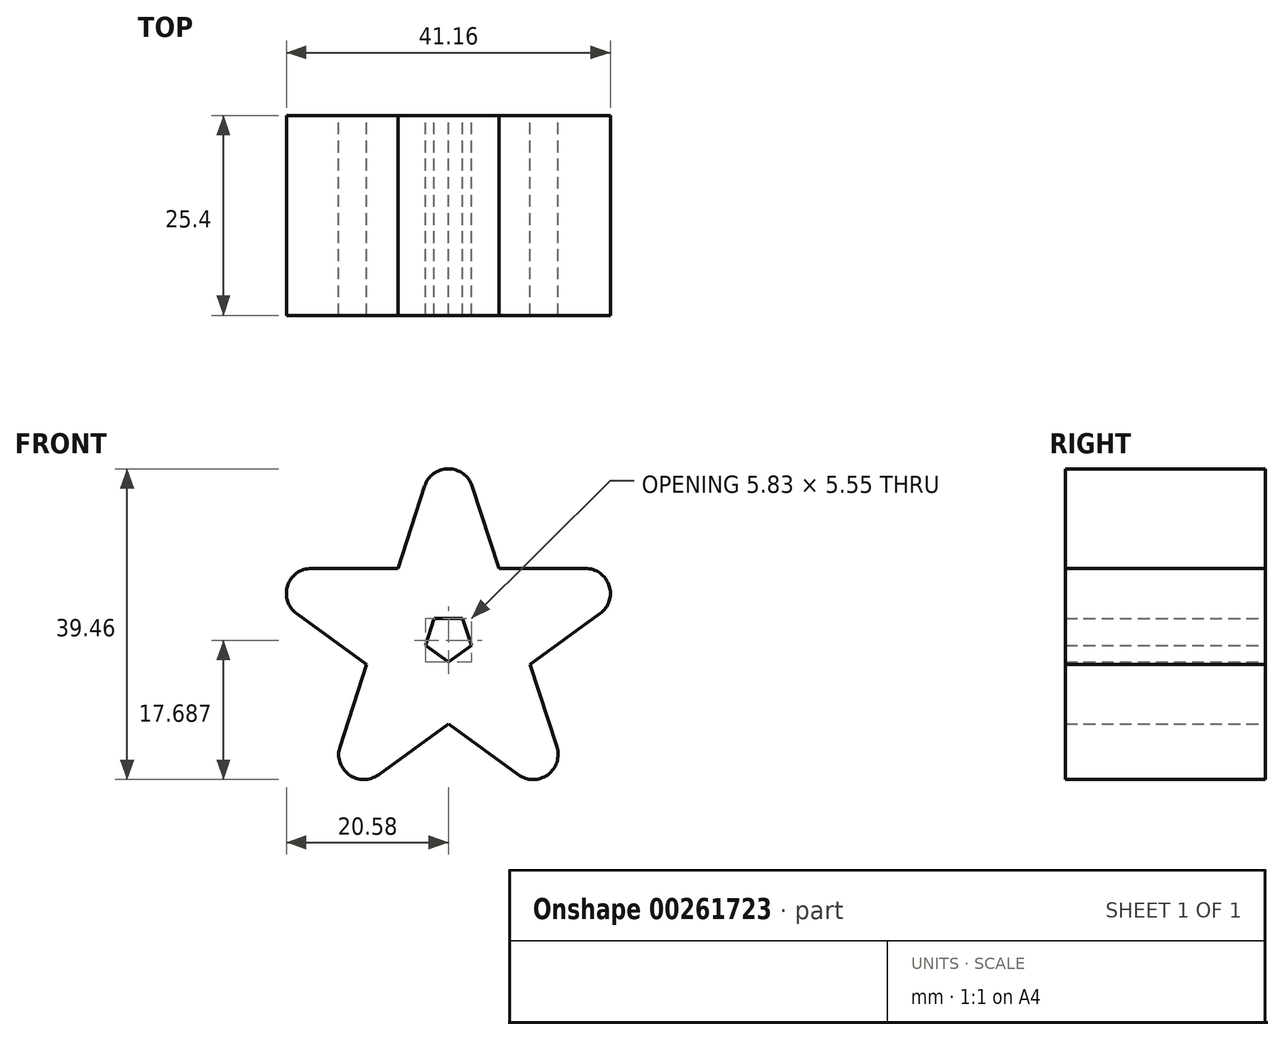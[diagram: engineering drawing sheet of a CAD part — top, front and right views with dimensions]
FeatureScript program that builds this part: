
annotation { "Feature Type Name" : "Feature", "Feature Type Description" : "" }
export const myFeature = defineFeature(function(context is Context, id is Id, definition is map)
    precondition{}
    {
        {
            var Q0;
            Q0=qCreatedBy(makeId("Front.planeOp"),FACE);
            var sketch = newSketch(context, id + "F0", { "sketchPlane" : qUnion([Q0])});
            skCircle(sketch, "E0", {"center": v(0, 18.3) * mm, "radius": 3.18 * mm});
            skCircle(sketch, "E1", {"center": v(-10.76, -14.8) * mm, "radius": 3.18 * mm});
            skCircle(sketch, "E2", {"center": v(10.76, -14.8) * mm, "radius": 3.18 * mm});
            skCircle(sketch, "E3", {"center": v(-17.4, 5.66) * mm, "radius": 3.18 * mm});
            skCircle(sketch, "E4", {"center": v(17.4, 5.66) * mm, "radius": 3.18 * mm});
            skLineSegment(sketch, "E5", {"start": v(-3.02, 19.28) * mm, "end": v(-13.78, -13.82) * mm});
            skLineSegment(sketch, "E6", {"start": v(-7.74, -15.79) * mm, "end": v(3.02, 17.32) * mm});
            skLineSegment(sketch, "E7", {"start": v(7.74, -15.79) * mm, "end": v(-3.02, 17.32) * mm});
            skLineSegment(sketch, "E8", {"start": v(3.02, 19.28) * mm, "end": v(13.78, -13.82) * mm});
            skLineSegment(sketch, "E9", {"start": v(8.9, -17.37) * mm, "end": v(-19.27, 3.09) * mm});
            skLineSegment(sketch, "E10", {"start": v(-15.54, 8.22) * mm, "end": v(12.62, -12.24) * mm});
            skLineSegment(sketch, "E11", {"start": v(-17.4, 8.83) * mm, "end": v(17.4, 8.83) * mm});
            skLineSegment(sketch, "E12", {"start": v(-17.4, 2.48) * mm, "end": v(17.4, 2.48) * mm});
            skLineSegment(sketch, "E13", {"start": v(19.27, 3.09) * mm, "end": v(-8.9, -17.37) * mm});
            skLineSegment(sketch, "E14", {"start": v(-12.62, -12.24) * mm, "end": v(15.54, 8.22) * mm});
            skCircle(sketch, "E15", {"center": v(0, 0) * mm, "radius": 21.48 * mm});
            skCircle(sketch, "E16", {"center": v(0, 0) * mm, "radius": 28.58 * mm});
            skLineSegment(sketch, "E17", {"start": v(-3.02, 19.28) * mm, "end": v(0, 28.57) * mm});
            skLineSegment(sketch, "E18", {"start": v(3.02, 19.28) * mm, "end": v(0, 28.57) * mm});
            skSolve(sketch);
        }
        {
            var Q0;
            {var subQ0=sQuery(id+"F0.wireOp",EDGE,"E0");var subQ1=makeQuery(id+"F0.imprint","INTERSECT",VERTEX,{"derivedFrom":[subQ0,sQuery(id+"F0.wireOp",EDGE,"E6")]});Q0=makeQuery(id+"F0.imprint","IMPRINT",FACE,{"disambiguationData":[TD([[makeQuery(id+"F0.imprint","IMPRINT",EDGE,{"disambiguationData":[TD([[subQ1,1.0]])],"derivedFrom":subQ0}),1.0]])]});}
            var Q1;
            {var subQ0=sQuery(id+"F0.wireOp",EDGE,"E6");var subQ1=sQuery(id+"F0.wireOp",EDGE,"E0");var subQ2=makeQuery(id+"F0.imprint","INTERSECT",VERTEX,{"derivedFrom":[subQ1,subQ0]});Q1=makeQuery(id+"F0.imprint","IMPRINT",FACE,{"disambiguationData":[TD([[makeQuery(id+"F0.imprint","IMPRINT",EDGE,{"disambiguationData":[TD([[subQ2,1.0]])],"derivedFrom":subQ1}),-1.0]])]});}
            var Q2;
            {var subQ1=sQuery(id+"F0.wireOp",EDGE,"E0");var subQ3=sQuery(id+"F0.wireOp",EDGE,"E7");var subQ4=makeQuery(id+"F0.imprint","INTERSECT",VERTEX,{"derivedFrom":[subQ1,subQ3]});Q2=makeQuery(id+"F0.imprint","IMPRINT",FACE,{"disambiguationData":[TD([[makeQuery(id+"F0.imprint","IMPRINT",EDGE,{"disambiguationData":[TD([[subQ4,1.0]])],"derivedFrom":subQ3}),1.0]])]});}
            var Q3;
            {var subQ1=sQuery(id+"F0.wireOp",EDGE,"E5");var subQ8=sQuery(id+"F0.wireOp",EDGE,"E11");var subQ11=makeQuery(id+"F0.imprint","INTERSECT",VERTEX,{"derivedFrom":[subQ1,subQ8]});Q3=makeQuery(id+"F0.imprint","IMPRINT",FACE,{"disambiguationData":[TD([[makeQuery(id+"F0.imprint","IMPRINT",EDGE,{"disambiguationData":[TD([[subQ11,-1.0]])],"derivedFrom":subQ1}),1.0]])]});}
            var Q4;
            {var subQ0=sQuery(id+"F0.wireOp",EDGE,"E10");var subQ1=sQuery(id+"F0.wireOp",EDGE,"E6");var subQ2=makeQuery(id+"F0.imprint","INTERSECT",VERTEX,{"derivedFrom":[subQ1,subQ0]});Q4=makeQuery(id+"F0.imprint","IMPRINT",FACE,{"disambiguationData":[TD([[makeQuery(id+"F0.imprint","IMPRINT",EDGE,{"disambiguationData":[TD([[subQ2,-1.0]])],"derivedFrom":subQ1}),1.0]])]});}
            var Q5;
            {var subQ3=sQuery(id+"F0.wireOp",EDGE,"E12");var subQ5=sQuery(id+"F0.wireOp",EDGE,"E5");var subQ6=makeQuery(id+"F0.imprint","INTERSECT",VERTEX,{"derivedFrom":[subQ5,subQ3]});Q5=makeQuery(id+"F0.imprint","IMPRINT",FACE,{"disambiguationData":[TD([[makeQuery(id+"F0.imprint","IMPRINT",EDGE,{"disambiguationData":[TD([[subQ6,-1.0]])],"derivedFrom":subQ5}),1.0]])]});}
            var Q6;
            {var subQ0=sQuery(id+"F0.wireOp",EDGE,"E5");var subQ1=sQuery(id+"F0.wireOp",EDGE,"E1");var subQ2=makeQuery(id+"F0.imprint","INTERSECT",VERTEX,{"derivedFrom":[subQ1,subQ0]});Q6=makeQuery(id+"F0.imprint","IMPRINT",FACE,{"disambiguationData":[TD([[makeQuery(id+"F0.imprint","IMPRINT",EDGE,{"disambiguationData":[TD([[subQ2,1.0]])],"derivedFrom":subQ1}),-1.0]])]});}
            var Q7;
            {var subQ0=sQuery(id+"F0.wireOp",EDGE,"E6");var subQ1=sQuery(id+"F0.wireOp",EDGE,"E1");var subQ2=makeQuery(id+"F0.imprint","INTERSECT",VERTEX,{"derivedFrom":[subQ1,subQ0]});Q7=makeQuery(id+"F0.imprint","IMPRINT",FACE,{"disambiguationData":[TD([[makeQuery(id+"F0.imprint","IMPRINT",EDGE,{"disambiguationData":[TD([[subQ2,-1.0]])],"derivedFrom":subQ1}),-1.0]])]});}
            var Q8;
            {var subQ0=sQuery(id+"F0.wireOp",EDGE,"E1");var subQ4=makeQuery(id+"F0.imprint","INTERSECT",VERTEX,{"derivedFrom":[subQ0,sQuery(id+"F0.wireOp",EDGE,"E5")]});Q8=makeQuery(id+"F0.imprint","IMPRINT",FACE,{"disambiguationData":[TD([[makeQuery(id+"F0.imprint","IMPRINT",EDGE,{"disambiguationData":[TD([[subQ4,1.0]])],"derivedFrom":subQ0}),1.0]])]});}
            var Q9;
            {var subQ0=sQuery(id+"F0.wireOp",EDGE,"E7");var subQ1=sQuery(id+"F0.wireOp",EDGE,"E6");var subQ2=makeQuery(id+"F0.imprint","INTERSECT",VERTEX,{"derivedFrom":[subQ1,subQ0]});Q9=makeQuery(id+"F0.imprint","IMPRINT",FACE,{"disambiguationData":[TD([[makeQuery(id+"F0.imprint","IMPRINT",EDGE,{"disambiguationData":[TD([[subQ2,-1.0]])],"derivedFrom":subQ1}),1.0]])]});}
            var Q10;
            {var subQ0=sQuery(id+"F0.wireOp",EDGE,"E9");var subQ1=sQuery(id+"F0.wireOp",EDGE,"E6");var subQ2=makeQuery(id+"F0.imprint","INTERSECT",VERTEX,{"derivedFrom":[subQ1,subQ0]});Q10=makeQuery(id+"F0.imprint","IMPRINT",FACE,{"disambiguationData":[TD([[makeQuery(id+"F0.imprint","IMPRINT",EDGE,{"disambiguationData":[TD([[subQ2,-1.0]])],"derivedFrom":subQ1}),1.0]])]});}
            var Q11;
            {var subQ0=sQuery(id+"F0.wireOp",EDGE,"E10");var subQ1=sQuery(id+"F0.wireOp",EDGE,"E5");var subQ2=makeQuery(id+"F0.imprint","INTERSECT",VERTEX,{"derivedFrom":[subQ1,subQ0]});Q11=makeQuery(id+"F0.imprint","IMPRINT",FACE,{"disambiguationData":[TD([[makeQuery(id+"F0.imprint","IMPRINT",EDGE,{"disambiguationData":[TD([[subQ2,-1.0]])],"derivedFrom":subQ1}),1.0]])]});}
            extrude(context, id + "F1", {"entities" : qUnion([Q0, Q1, Q2, Q3, Q4, Q5, Q6, Q7, Q8, Q9, Q10, Q11]), "depth" : 25.4 * mm});
        }
        {
            var Q0;
            {var subQ0=sQuery(id+"F0.wireOp",EDGE,"E3");var subQ5=makeQuery(id+"F0.imprint","INTERSECT",VERTEX,{"derivedFrom":[subQ0,sQuery(id+"F0.wireOp",EDGE,"E10")]});Q0=makeQuery(id+"F0.imprint","IMPRINT",FACE,{"disambiguationData":[TD([[makeQuery(id+"F0.imprint","IMPRINT",EDGE,{"disambiguationData":[TD([[subQ5,-1.0]])],"derivedFrom":subQ0}),1.0]])]});}
            var Q1;
            {var subQ0=sQuery(id+"F0.wireOp",EDGE,"E10");var subQ1=sQuery(id+"F0.wireOp",EDGE,"E3");var subQ2=makeQuery(id+"F0.imprint","INTERSECT",VERTEX,{"derivedFrom":[subQ1,subQ0]});Q1=makeQuery(id+"F0.imprint","IMPRINT",FACE,{"disambiguationData":[TD([[makeQuery(id+"F0.imprint","IMPRINT",EDGE,{"disambiguationData":[TD([[subQ2,-1.0]])],"derivedFrom":subQ1}),-1.0]])]});}
            var Q2;
            {var subQ0=sQuery(id+"F0.wireOp",EDGE,"E10");var subQ1=sQuery(id+"F0.wireOp",EDGE,"E3");var subQ2=makeQuery(id+"F0.imprint","INTERSECT",VERTEX,{"derivedFrom":[subQ1,subQ0]});Q2=makeQuery(id+"F0.imprint","IMPRINT",FACE,{"disambiguationData":[TD([[makeQuery(id+"F0.imprint","IMPRINT",EDGE,{"disambiguationData":[TD([[subQ2,1.0]])],"derivedFrom":subQ1}),-1.0]])]});}
            var Q3;
            {var subQ0=sQuery(id+"F0.wireOp",EDGE,"E12");var subQ1=sQuery(id+"F0.wireOp",EDGE,"E6");var subQ2=makeQuery(id+"F0.imprint","INTERSECT",VERTEX,{"derivedFrom":[subQ1,subQ0]});Q3=makeQuery(id+"F0.imprint","IMPRINT",FACE,{"disambiguationData":[TD([[makeQuery(id+"F0.imprint","IMPRINT",EDGE,{"disambiguationData":[TD([[subQ2,-1.0]])],"derivedFrom":subQ1}),-1.0]])]});}
            var Q4;
            {var subQ1=sQuery(id+"F0.wireOp",EDGE,"E6");var subQ5=sQuery(id+"F0.wireOp",EDGE,"E7");var subQ6=makeQuery(id+"F0.imprint","INTERSECT",VERTEX,{"derivedFrom":[subQ1,subQ5]});Q4=makeQuery(id+"F0.imprint","IMPRINT",FACE,{"disambiguationData":[TD([[makeQuery(id+"F0.imprint","IMPRINT",EDGE,{"disambiguationData":[TD([[subQ6,-1.0]])],"derivedFrom":subQ1}),-1.0]])]});}
            var Q5;
            {var subQ0=sQuery(id+"F0.wireOp",EDGE,"E11");var subQ1=sQuery(id+"F0.wireOp",EDGE,"E4");var subQ2=makeQuery(id+"F0.imprint","INTERSECT",VERTEX,{"derivedFrom":[subQ1,subQ0]});Q5=makeQuery(id+"F0.imprint","IMPRINT",FACE,{"disambiguationData":[TD([[makeQuery(id+"F0.imprint","IMPRINT",EDGE,{"disambiguationData":[TD([[subQ2,-1.0]])],"derivedFrom":subQ1}),-1.0]])]});}
            var Q6;
            {var subQ0=sQuery(id+"F0.wireOp",EDGE,"E12");var subQ1=sQuery(id+"F0.wireOp",EDGE,"E4");var subQ2=makeQuery(id+"F0.imprint","INTERSECT",VERTEX,{"derivedFrom":[subQ1,subQ0]});Q6=makeQuery(id+"F0.imprint","IMPRINT",FACE,{"disambiguationData":[TD([[makeQuery(id+"F0.imprint","IMPRINT",EDGE,{"disambiguationData":[TD([[subQ2,1.0]])],"derivedFrom":subQ1}),-1.0]])]});}
            var Q7;
            {var subQ0=sQuery(id+"F0.wireOp",EDGE,"E4");var subQ4=makeQuery(id+"F0.imprint","INTERSECT",VERTEX,{"derivedFrom":[subQ0,sQuery(id+"F0.wireOp",EDGE,"E11")]});Q7=makeQuery(id+"F0.imprint","IMPRINT",FACE,{"disambiguationData":[TD([[makeQuery(id+"F0.imprint","IMPRINT",EDGE,{"disambiguationData":[TD([[subQ4,1.0]])],"derivedFrom":subQ0}),1.0]])]});}
            var Q8;
            {var subQ0=sQuery(id+"F0.wireOp",EDGE,"E14");var subQ1=sQuery(id+"F0.wireOp",EDGE,"E8");var subQ2=makeQuery(id+"F0.imprint","INTERSECT",VERTEX,{"derivedFrom":[subQ1,subQ0]});Q8=makeQuery(id+"F0.imprint","IMPRINT",FACE,{"disambiguationData":[TD([[makeQuery(id+"F0.imprint","IMPRINT",EDGE,{"disambiguationData":[TD([[subQ2,-1.0]])],"derivedFrom":subQ1}),-1.0]])]});}
            extrude(context, id + "F2", {"entities" : qUnion([Q0, Q1, Q2, Q3, Q4, Q5, Q6, Q7, Q8]), "operationType" : NewBodyOperationType.ADD, "depth" : 25.4 * mm});
        }
        {
            var Q0;
            {var subQ0=sQuery(id+"F0.wireOp",EDGE,"E6");var subQ1=sQuery(id+"F0.wireOp",EDGE,"E0");var subQ2=makeQuery(id+"F0.imprint","INTERSECT",VERTEX,{"derivedFrom":[subQ1,subQ0]});Q0=makeQuery(id+"F0.imprint","IMPRINT",FACE,{"disambiguationData":[TD([[makeQuery(id+"F0.imprint","IMPRINT",EDGE,{"disambiguationData":[TD([[subQ2,1.0]])],"derivedFrom":subQ0}),-1.0]])]});}
            var Q1;
            {var subQ0=sQuery(id+"F0.wireOp",EDGE,"E14");var subQ1=sQuery(id+"F0.wireOp",EDGE,"E7");var subQ2=makeQuery(id+"F0.imprint","INTERSECT",VERTEX,{"derivedFrom":[subQ1,subQ0]});Q1=makeQuery(id+"F0.imprint","IMPRINT",FACE,{"disambiguationData":[TD([[makeQuery(id+"F0.imprint","IMPRINT",EDGE,{"disambiguationData":[TD([[subQ2,-1.0]])],"derivedFrom":subQ1}),-1.0]])]});}
            var Q2;
            {var subQ5=sQuery(id+"F0.wireOp",EDGE,"E7");var subQ9=sQuery(id+"F0.wireOp",EDGE,"E10");var subQ10=makeQuery(id+"F0.imprint","INTERSECT",VERTEX,{"derivedFrom":[subQ5,subQ9]});Q2=makeQuery(id+"F0.imprint","IMPRINT",FACE,{"disambiguationData":[TD([[makeQuery(id+"F0.imprint","IMPRINT",EDGE,{"disambiguationData":[TD([[subQ10,-1.0]])],"derivedFrom":subQ5}),-1.0]])]});}
            var Q3;
            {var subQ0=sQuery(id+"F0.wireOp",EDGE,"E8");var subQ1=sQuery(id+"F0.wireOp",EDGE,"E2");var subQ2=makeQuery(id+"F0.imprint","INTERSECT",VERTEX,{"derivedFrom":[subQ1,subQ0]});Q3=makeQuery(id+"F0.imprint","IMPRINT",FACE,{"disambiguationData":[TD([[makeQuery(id+"F0.imprint","IMPRINT",EDGE,{"disambiguationData":[TD([[subQ2,-1.0]])],"derivedFrom":subQ1}),-1.0]])]});}
            var Q4;
            {var subQ0=sQuery(id+"F0.wireOp",EDGE,"E7");var subQ1=sQuery(id+"F0.wireOp",EDGE,"E2");var subQ2=makeQuery(id+"F0.imprint","INTERSECT",VERTEX,{"derivedFrom":[subQ1,subQ0]});Q4=makeQuery(id+"F0.imprint","IMPRINT",FACE,{"disambiguationData":[TD([[makeQuery(id+"F0.imprint","IMPRINT",EDGE,{"disambiguationData":[TD([[subQ2,1.0]])],"derivedFrom":subQ1}),-1.0]])]});}
            var Q5;
            {var subQ0=sQuery(id+"F0.wireOp",EDGE,"E2");var subQ5=makeQuery(id+"F0.imprint","INTERSECT",VERTEX,{"derivedFrom":[subQ0,sQuery(id+"F0.wireOp",EDGE,"E8")]});Q5=makeQuery(id+"F0.imprint","IMPRINT",FACE,{"disambiguationData":[TD([[makeQuery(id+"F0.imprint","IMPRINT",EDGE,{"disambiguationData":[TD([[subQ5,-1.0]])],"derivedFrom":subQ0}),1.0]])]});}
            var Q6;
            {var subQ0=sQuery(id+"F0.wireOp",EDGE,"E13");var subQ1=sQuery(id+"F0.wireOp",EDGE,"E7");var subQ2=makeQuery(id+"F0.imprint","INTERSECT",VERTEX,{"derivedFrom":[subQ1,subQ0]});Q6=makeQuery(id+"F0.imprint","IMPRINT",FACE,{"disambiguationData":[TD([[makeQuery(id+"F0.imprint","IMPRINT",EDGE,{"disambiguationData":[TD([[subQ2,-1.0]])],"derivedFrom":subQ1}),-1.0]])]});}
            extrude(context, id + "F3", {"entities" : qUnion([Q0, Q1, Q2, Q3, Q4, Q5, Q6]), "operationType" : NewBodyOperationType.ADD, "depth" : 25.4 * mm});
        }
        {
            var Q0;
            {var subQ0=sQuery(id+"F0.wireOp",EDGE,"E6");var subQ1=sQuery(id+"F0.wireOp",EDGE,"E1");var subQ2=makeQuery(id+"F0.imprint","INTERSECT",VERTEX,{"derivedFrom":[subQ1,subQ0]});Q0=makeQuery(id+"F0.imprint","IMPRINT",FACE,{"disambiguationData":[TD([[makeQuery(id+"F0.imprint","IMPRINT",EDGE,{"disambiguationData":[TD([[subQ2,1.0]])],"derivedFrom":subQ1}),-1.0]])]});}
            var Q1;
            {var subQ0=sQuery(id+"F0.wireOp",EDGE,"E9");var subQ1=sQuery(id+"F0.wireOp",EDGE,"E6");var subQ2=makeQuery(id+"F0.imprint","INTERSECT",VERTEX,{"derivedFrom":[subQ1,subQ0]});Q1=makeQuery(id+"F0.imprint","IMPRINT",FACE,{"disambiguationData":[TD([[makeQuery(id+"F0.imprint","IMPRINT",EDGE,{"disambiguationData":[TD([[subQ2,-1.0]])],"derivedFrom":subQ1}),-1.0]])]});}
            var Q2;
            {var subQ0=sQuery(id+"F0.wireOp",EDGE,"E10");var subQ1=sQuery(id+"F0.wireOp",EDGE,"E7");var subQ2=makeQuery(id+"F0.imprint","INTERSECT",VERTEX,{"derivedFrom":[subQ1,subQ0]});Q2=makeQuery(id+"F0.imprint","IMPRINT",FACE,{"disambiguationData":[TD([[makeQuery(id+"F0.imprint","IMPRINT",EDGE,{"disambiguationData":[TD([[subQ2,-1.0]])],"derivedFrom":subQ1}),1.0]])]});}
            var Q3;
            {var subQ0=sQuery(id+"F0.wireOp",EDGE,"E12");var subQ1=sQuery(id+"F0.wireOp",EDGE,"E4");var subQ2=makeQuery(id+"F0.imprint","INTERSECT",VERTEX,{"derivedFrom":[subQ1,subQ0]});Q3=makeQuery(id+"F0.imprint","IMPRINT",FACE,{"disambiguationData":[TD([[makeQuery(id+"F0.imprint","IMPRINT",EDGE,{"disambiguationData":[TD([[subQ2,-1.0]])],"derivedFrom":subQ1}),-1.0]])]});}
            extrude(context, id + "F4", {"entities" : qUnion([Q0, Q1, Q2, Q3]), "operationType" : NewBodyOperationType.ADD, "depth" : 25.4 * mm});
        }
        {
            var Q0;
            {var subQ0=sQuery(id+"F0.wireOp",EDGE,"E9");var subQ1=sQuery(id+"F0.wireOp",EDGE,"E3");var subQ2=makeQuery(id+"F0.imprint","INTERSECT",VERTEX,{"derivedFrom":[subQ1,subQ0]});Q0=makeQuery(id+"F0.imprint","IMPRINT",FACE,{"disambiguationData":[TD([[makeQuery(id+"F0.imprint","IMPRINT",EDGE,{"disambiguationData":[TD([[subQ2,-1.0]])],"derivedFrom":subQ1}),-1.0]])]});}
            var Q1;
            {var subQ0=sQuery(id+"F0.wireOp",EDGE,"E14");var subQ1=sQuery(id+"F0.wireOp",EDGE,"E6");var subQ2=makeQuery(id+"F0.imprint","INTERSECT",VERTEX,{"derivedFrom":[subQ1,subQ0]});Q1=makeQuery(id+"F0.imprint","IMPRINT",FACE,{"disambiguationData":[TD([[makeQuery(id+"F0.imprint","IMPRINT",EDGE,{"disambiguationData":[TD([[subQ2,-1.0]])],"derivedFrom":subQ1}),-1.0]])]});}
            var Q2;
            {var subQ0=sQuery(id+"F0.wireOp",EDGE,"E7");var subQ1=sQuery(id+"F0.wireOp",EDGE,"E2");var subQ2=makeQuery(id+"F0.imprint","INTERSECT",VERTEX,{"derivedFrom":[subQ1,subQ0]});Q2=makeQuery(id+"F0.imprint","IMPRINT",FACE,{"disambiguationData":[TD([[makeQuery(id+"F0.imprint","IMPRINT",EDGE,{"disambiguationData":[TD([[subQ2,-1.0]])],"derivedFrom":subQ1}),-1.0]])]});}
            extrude(context, id + "F5", {"entities" : qUnion([Q0, Q1, Q2]), "operationType" : NewBodyOperationType.ADD, "depth" : 25.4 * mm});
        }
    });
